# Revit family: Seat_Cover_Dispenser-Bobrick-TrimLineSeries-B-3013
name_source: partatom
category: Specialty Equipment
revit_build: Autodesk Revit 2018 (Build: 20170223_1515(x64)
units: mm (PartAtom-declared; Revit-internal decimal feet)

## family parameters
Cut with Voids When Loaded = No
Host = Face
OmniClass Number = 23.40.20.21
OmniClass Title = Toilet and Bath Specialties
Part Type = Normal
Room Calculation Point = No
Round Connector Dimension = Use Diameter
Shared = Yes

## types (1)
- B-3013
    ADA = Yes
    ADA Compliant = Yes
    Assembly Code = C1030200
    Cabinet Material = Metal-Bobrick-Stainless Steel
    Capacity = 500 toilet seat covers
    Default Elevation = 0"
    Description = Recessed Toilet Seat-Cover Dispenser
    Door Material = Stainless Steel-Bobrick-Satin
    Height = 13 1/16"
    Installation Type = Recessed Wal Mounted
    Length = 17 9/16"
    Manufacturer = Bobrick
    Material = Stainless Steel-Bobrick-Satin
    Model = B-3013
    Mounting Height Constraint = 41 7/8"
    Price = Prices may vary. Please consult Manufacturer Representative for most up-to-date price list.
    Product Documentation Link = https://www.bobrick.com
    Product Page URL = https://www.bobrick.com
    Revised Date = 10/15/2021
    Rough Wall Opening Depth = 2 3/4"
    Rough Wall Opening Height = 11 7/16"
    Rough Wall Opening Width = 15 7/8"
    URL = http://www.bobrick.com
    Width = 2 15/16"

## geometry (parser evidence)
native form markers: Sweep x3
no freeform markers — native parametric forms only
